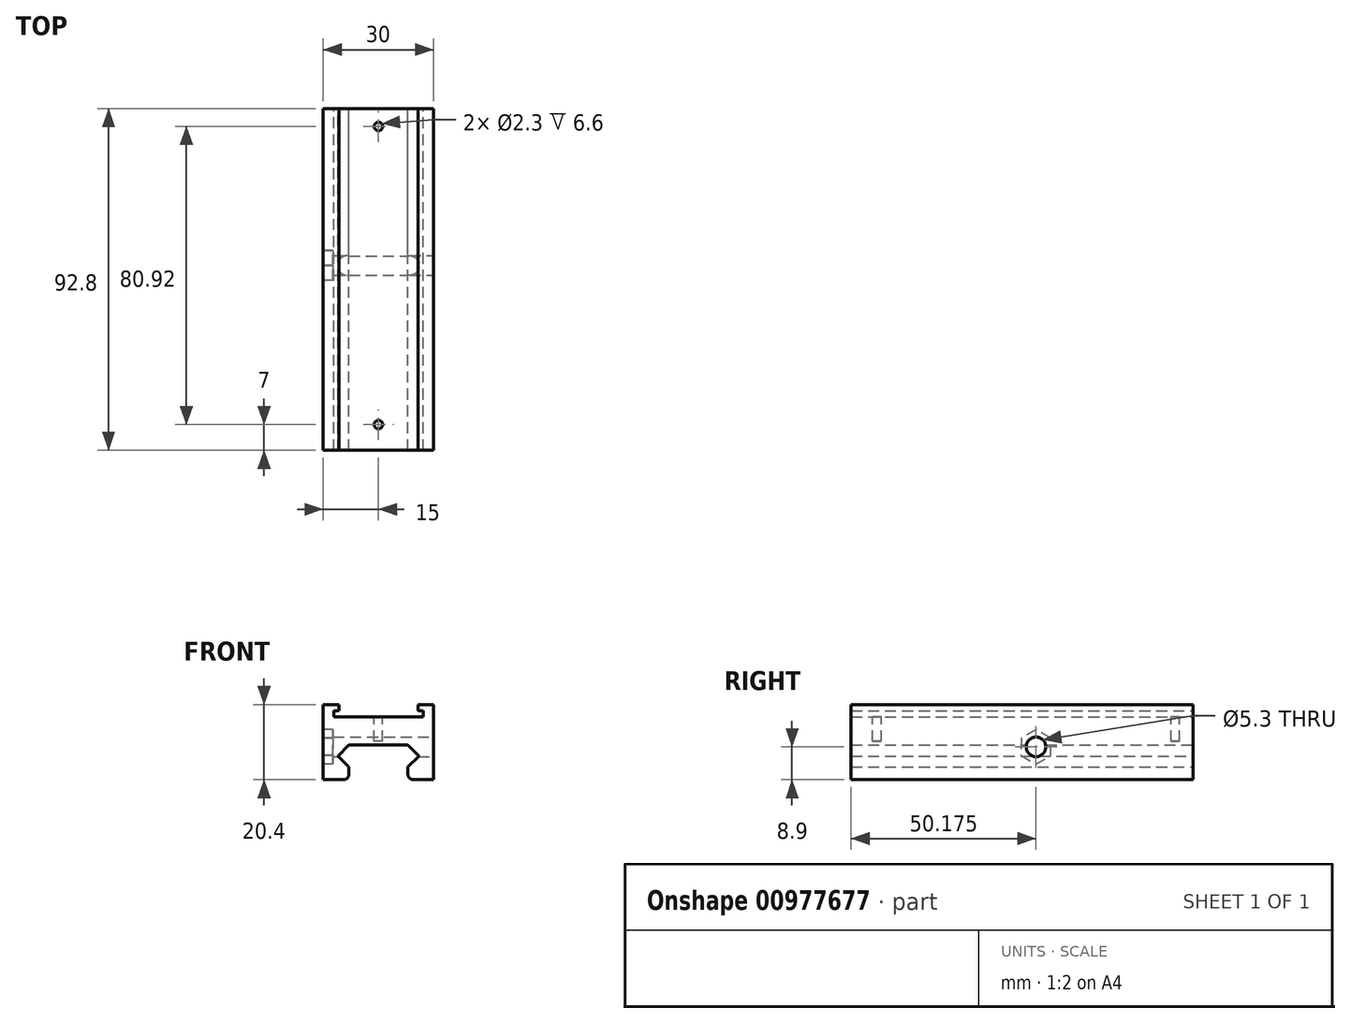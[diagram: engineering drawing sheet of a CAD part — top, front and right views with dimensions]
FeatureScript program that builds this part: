
annotation { "Feature Type Name" : "Feature", "Feature Type Description" : "" }
export const myFeature = defineFeature(function(context is Context, id is Id, definition is map)
    precondition{}
    {
        {
            var Q0;
            Q0=qCreatedBy(makeId("Front.planeOp"),FACE);
            var sketch = newSketch(context, id + "F0", { "sketchPlane" : qUnion([Q0])});
            skLineSegment(sketch, "E0", {"start": v(-15, 0) * mm, "end": v(-9.5, 0) * mm});
            skLineSegment(sketch, "E1", {"start": v(-8, 1.5) * mm, "end": v(-8, 3.4) * mm});
            skLineSegment(sketch, "E2", {"start": v(-8, 3.4) * mm, "end": v(-11, 6.4) * mm});
            skLineSegment(sketch, "E3", {"start": v(-11, 6.4) * mm, "end": v(-8, 9.4) * mm});
            skLineSegment(sketch, "E4", {"start": v(-8, 9.4) * mm, "end": v(0, 9.4) * mm});
            skLineSegment(sketch, "E5", {"start": v(-9.5, 7.9) * mm, "end": v(-9.5, 4.9) * mm});
            skLineSegment(sketch, "E6", {"start": v(-9.5, 4.9) * mm, "end": v(0, 4.9) * mm});
            skLineSegment(sketch, "E7", {"start": v(-9.5, 7.9) * mm, "end": v(0, 7.9) * mm});
            skPoint(sketch, "E8.visualSharp", {"position": v(-8, 0) * mm});
            skArc(sketch, "E8.filletArc", {"start": v(-9.5, 0) * mm, "mid": v(-8.44, 0.44) * mm, "end": v(-8, 1.5) * mm});
            skLineSegment(sketch, "E9.MirrorCS", {"start": v(8, 9.4) * mm, "end": v(0, 9.4) * mm});
            skLineSegment(sketch, "E10.MirrorCS", {"start": v(11, 6.4) * mm, "end": v(8, 9.4) * mm});
            skLineSegment(sketch, "E11.MirrorCS", {"start": v(8, 3.4) * mm, "end": v(11, 6.4) * mm});
            skLineSegment(sketch, "E12.MirrorCS", {"start": v(8, 1.5) * mm, "end": v(8, 3.4) * mm});
            skArc(sketch, "E13.MirrorCS", {"start": v(9.5, 0) * mm, "mid": v(8.44, 0.44) * mm, "end": v(8, 1.5) * mm});
            skLineSegment(sketch, "E14.MirrorCS", {"start": v(15, 0) * mm, "end": v(9.5, 0) * mm});
            skLineSegment(sketch, "E15", {"start": v(-15, 0) * mm, "end": v(-15, 20.4) * mm});
            skLineSegment(sketch, "E16", {"start": v(-15, 20.4) * mm, "end": v(0, 20.4) * mm});
            skLineSegment(sketch, "E17.MirrorCS", {"start": v(15, 20.4) * mm, "end": v(0, 20.4) * mm});
            skLineSegment(sketch, "E18.MirrorCS", {"start": v(15, 0) * mm, "end": v(15, 20.4) * mm});
            skPoint(sketch, "E19.orphan", {"position": v(-33.3, 0) * mm});
            skPoint(sketch, "E20.orphan", {"position": v(33.3, 0) * mm});
            skSolve(sketch);
        }
        {
            var Q0;
            Q0=makeQuery(id+"F0.imprint","IMPRINT",FACE,{"disambiguationData":[TD([[makeQuery(id+"F0.imprint","IMPRINT",EDGE,{"derivedFrom":sQuery(id+"F0.wireOp",EDGE,"E0")}),1.0]])]});
            extrude(context, id + "F1", {"entities" : qUnion([Q0]), "depth" : 92.8 * mm, "offsetDistance" : 25 * mm});
        }
        {
            var Q0;
            Q0=makeQuery(id+"F1.opExtrude","CAP_FACE",FACE,{"disambiguationData":[OSD([sQuery(id+"F0.wireOp",EDGE,"E0"),sQuery(id+"F0.wireOp",EDGE,"E1"),sQuery(id+"F0.wireOp",EDGE,"E2"),sQuery(id+"F0.wireOp",EDGE,"E3"),sQuery(id+"F0.wireOp",EDGE,"E4"),sQuery(id+"F0.wireOp",EDGE,"E5"),sQuery(id+"F0.wireOp",EDGE,"E8.filletArc"),sQuery(id+"F0.wireOp",EDGE,"E9.MirrorCS"),sQuery(id+"F0.wireOp",EDGE,"E10.MirrorCS"),sQuery(id+"F0.wireOp",EDGE,"E11.MirrorCS"),sQuery(id+"F0.wireOp",EDGE,"E12.MirrorCS"),sQuery(id+"F0.wireOp",EDGE,"E13.MirrorCS"),sQuery(id+"F0.wireOp",EDGE,"E14.MirrorCS"),sQuery(id+"F0.wireOp",EDGE,"E15"),sQuery(id+"F0.wireOp",EDGE,"E16"),sQuery(id+"F0.wireOp",EDGE,"E17.MirrorCS"),sQuery(id+"F0.wireOp",EDGE,"E18.MirrorCS")])],"isStart":true});
            var sketch = newSketch(context, id + "F2", { "sketchPlane" : qUnion([Q0])});
            skLineSegment(sketch, "E21", {"start": v(-10.75, 20.4) * mm, "end": v(-10.75, 18.75) * mm});
            skLineSegment(sketch, "E22", {"start": v(-10.75, 18.75) * mm, "end": v(-12.1, 18.75) * mm});
            skLineSegment(sketch, "E23", {"start": v(-12.1, 18.75) * mm, "end": v(-12.1, 17) * mm});
            skLineSegment(sketch, "E24", {"start": v(-12.1, 17) * mm, "end": v(0, 17) * mm});
            skLineSegment(sketch, "E25", {"start": v(-10.75, 20.4) * mm, "end": v(0, 20.4) * mm});
            skLineSegment(sketch, "E26.MirrorCS", {"start": v(10.75, 20.4) * mm, "end": v(0, 20.4) * mm});
            skLineSegment(sketch, "E27.MirrorCS", {"start": v(10.75, 20.4) * mm, "end": v(10.75, 18.75) * mm});
            skLineSegment(sketch, "E28.MirrorCS", {"start": v(12.1, 18.75) * mm, "end": v(12.1, 17) * mm});
            skLineSegment(sketch, "E29.MirrorCS", {"start": v(12.1, 17) * mm, "end": v(0, 17) * mm});
            skLineSegment(sketch, "E30.MirrorCS", {"start": v(10.75, 18.75) * mm, "end": v(12.1, 18.75) * mm});
            skSolve(sketch);
        }
        {
            var Q0;
            Q0=makeQuery(id+"F2.imprint","IMPRINT",FACE,{"disambiguationData":[TD([[makeQuery(id+"F2.imprint","IMPRINT",EDGE,{"derivedFrom":sQuery(id+"F2.wireOp",EDGE,"E21")}),1.0]])]});
            var Q1;
            Q1=makeQuery(id+"F1.opExtrude","CAP_FACE",FACE,{"disambiguationData":[OSD([sQuery(id+"F0.wireOp",EDGE,"E0"),sQuery(id+"F0.wireOp",EDGE,"E1"),sQuery(id+"F0.wireOp",EDGE,"E2"),sQuery(id+"F0.wireOp",EDGE,"E3"),sQuery(id+"F0.wireOp",EDGE,"E4"),sQuery(id+"F0.wireOp",EDGE,"E8.filletArc"),sQuery(id+"F0.wireOp",EDGE,"E9.MirrorCS"),sQuery(id+"F0.wireOp",EDGE,"E10.MirrorCS"),sQuery(id+"F0.wireOp",EDGE,"E11.MirrorCS"),sQuery(id+"F0.wireOp",EDGE,"E12.MirrorCS"),sQuery(id+"F0.wireOp",EDGE,"E13.MirrorCS"),sQuery(id+"F0.wireOp",EDGE,"E14.MirrorCS"),sQuery(id+"F0.wireOp",EDGE,"E15"),sQuery(id+"F0.wireOp",EDGE,"E16"),sQuery(id+"F0.wireOp",EDGE,"E17.MirrorCS"),sQuery(id+"F0.wireOp",EDGE,"E18.MirrorCS")])],"isStart":false});
            extrude(context, id + "F3", {"entities" : qUnion([Q0]), "operationType" : NewBodyOperationType.REMOVE, "endBound" : BoundingType.UP_TO_SURFACE, "oppositeDirection" : true, "depth" : 25 * mm, "endBoundEntityFace" : qUnion([Q1]), "offsetDistance" : 25 * mm});
        }
        {
            var Q0;
            Q0=makeQuery(id+"F3.boolean.opBoolean","COPY",FACE,{"derivedFrom":makeQuery(id+"F3.opExtrude","SWEPT_FACE",FACE,{"disambiguationData":[OSD([sQuery(id+"F2.wireOp",EDGE,"E24"),sQuery(id+"F2.wireOp",EDGE,"E29.MirrorCS")])]})});
            var sketch = newSketch(context, id + "F4", { "sketchPlane" : qUnion([Q0])});
            skCircle(sketch, "E31", {"center": v(0, -4.88) * mm, "radius": 1.15 * mm});
            skCircle(sketch, "E32", {"center": v(0, -85.8) * mm, "radius": 1.15 * mm});
            skSolve(sketch);
        }
        {
            var Q0;
            Q0 = qSketchRegion(id + "F4", true);
            extrude(context, id + "F5", {"entities" : qUnion([Q0]), "operationType" : NewBodyOperationType.REMOVE, "oppositeDirection" : true, "depth" : 6.6 * mm, "offsetDistance" : 25 * mm});
        }
        {
            var Q0;
            Q0=makeQuery(id+"F1.opExtrude","SWEPT_FACE",FACE,{"disambiguationData":[OSD([sQuery(id+"F0.wireOp",EDGE,"E18.MirrorCS")])]});
            var sketch = newSketch(context, id + "F6", { "sketchPlane" : qUnion([Q0])});
            skLineSegment(sketch, "E33", {"start": v(0, 6.4) * mm, "end": v(-92.8, 6.4) * mm, "construction": true});
            skCircle(sketch, "E34", {"center": v(-42.62, 8.9) * mm, "radius": 2.65 * mm});
            skSolve(sketch);
        }
        {
            var Q0;
            Q0 = qSketchRegion(id + "F6", true);
            extrude(context, id + "F7", {"entities" : qUnion([Q0]), "operationType" : NewBodyOperationType.REMOVE, "oppositeDirection" : true, "depth" : 30 * mm, "offsetDistance" : 25 * mm});
        }
        {
            var Q0;
            Q0=makeQuery(id+"F1.opExtrude","SWEPT_FACE",FACE,{"disambiguationData":[OSD([sQuery(id+"F0.wireOp",EDGE,"E15")])]});
            var sketch = newSketch(context, id + "F8", { "sketchPlane" : qUnion([Q0])});
            skCircle(sketch, "E35.cCircle", {"center": v(42.62, 8.9) * mm, "radius": 4.05 * mm, "construction": true});
            skLineSegment(sketch, "E35.0", {"start": v(42.53, 13.58) * mm, "end": v(46.63, 11.32) * mm});
            skLineSegment(sketch, "E35.1", {"start": v(46.63, 11.32) * mm, "end": v(46.72, 6.64) * mm});
            skLineSegment(sketch, "E35.2", {"start": v(46.72, 6.64) * mm, "end": v(42.72, 4.22) * mm});
            skLineSegment(sketch, "E35.3", {"start": v(42.72, 4.22) * mm, "end": v(38.62, 6.48) * mm});
            skLineSegment(sketch, "E35.4", {"start": v(38.62, 6.48) * mm, "end": v(38.53, 11.16) * mm});
            skLineSegment(sketch, "E35.5", {"start": v(38.53, 11.16) * mm, "end": v(42.53, 13.58) * mm});
            skPoint(sketch, "E35.0.midPoint", {"position": v(44.58, 12.45) * mm});
            skSolve(sketch);
        }
        {
            var Q0;
            Q0 = qSketchRegion(id + "F8", true);
            extrude(context, id + "F9", {"entities" : qUnion([Q0]), "operationType" : NewBodyOperationType.REMOVE, "oppositeDirection" : true, "depth" : 2.7 * mm, "offsetDistance" : 25 * mm});
        }
    });
